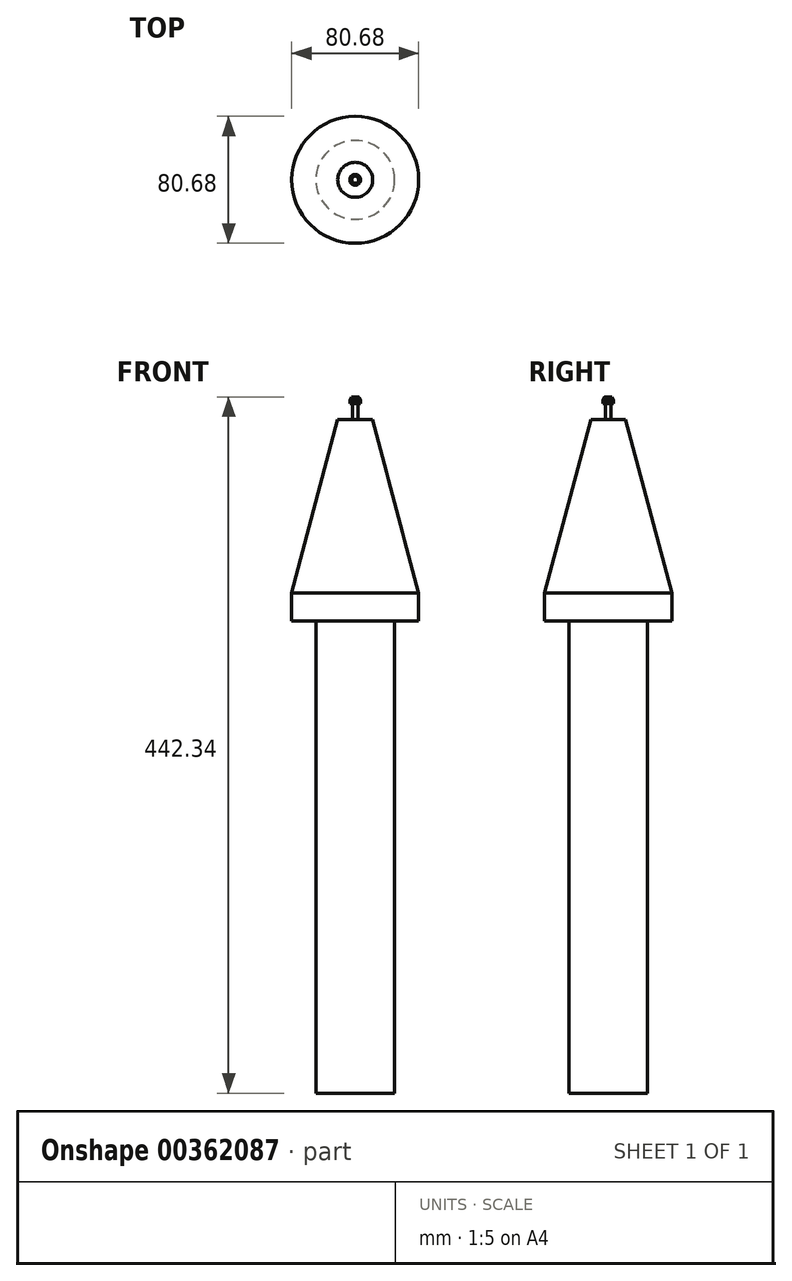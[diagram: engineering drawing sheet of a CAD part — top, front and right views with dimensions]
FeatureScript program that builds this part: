
annotation { "Feature Type Name" : "Feature", "Feature Type Description" : "" }
export const myFeature = defineFeature(function(context is Context, id is Id, definition is map)
    precondition{}
    {
        {
            var Q0;
            Q0=qCreatedBy(makeId("Front.planeOp"),FACE);
            var sketch = newSketch(context, id + "F0", { "sketchPlane" : qUnion([Q0])});
            skLineSegment(sketch, "E0", {"start": v(0, -215.17) * mm, "end": v(25, -215.17) * mm});
            skLineSegment(sketch, "E1", {"start": v(25, -215.17) * mm, "end": v(25, 84.83) * mm});
            skLineSegment(sketch, "E2", {"start": v(25, 84.83) * mm, "end": v(40.34, 84.83) * mm});
            skLineSegment(sketch, "E3", {"start": v(0, 212.9) * mm, "end": v(0, -215.17) * mm});
            skPoint(sketch, "E4.orphan", {"position": v(2.47, 236.47) * mm});
            skPoint(sketch, "E5.end.orphan", {"position": v(4.76, 236.47) * mm});
            skPoint(sketch, "E6.end.orphan", {"position": v(7.06, 236.47) * mm});
            skPoint(sketch, "E7.end.orphan", {"position": v(4.76, 212.9) * mm});
            skLineSegment(sketch, "E8", {"start": v(1.81, 212.9) * mm, "end": v(11.1, 212.9) * mm});
            skLineSegment(sketch, "E9", {"start": v(40.34, 102.43) * mm, "end": v(11.1, 212.9) * mm});
            skLineSegment(sketch, "E10", {"start": v(0, 227.17) * mm, "end": v(0, 212.9) * mm});
            skLineSegment(sketch, "E11", {"start": v(0, 227.17) * mm, "end": v(2.26, 227.17) * mm});
            skLineSegment(sketch, "E12", {"start": v(2.26, 227.17) * mm, "end": v(3.44, 224.95) * mm});
            skLineSegment(sketch, "E13", {"start": v(3.44, 224.95) * mm, "end": v(3.44, 222.87) * mm});
            skLineSegment(sketch, "E14", {"start": v(3.44, 222.87) * mm, "end": v(1.81, 222.87) * mm});
            skLineSegment(sketch, "E15", {"start": v(1.81, 222.87) * mm, "end": v(1.81, 212.9) * mm});
            skLineSegment(sketch, "E16", {"start": v(40.34, 84.83) * mm, "end": v(40.34, 102.43) * mm});
            skSolve(sketch);
        }
        {
            var Q0;
            Q0=makeQuery(id+"F0.imprint","IMPRINT",FACE,{"disambiguationData":[TD([[makeQuery(id+"F0.imprint","IMPRINT",EDGE,{"derivedFrom":sQuery(id+"F0.wireOp",EDGE,"E0")}),1.0]])]});
            var Q1;
            Q1=sQuery(id+"F0.wireOp",EDGE,"E3");
            revolve(context, id + "F1", {"entities" : qUnion([Q0]), "axis" : qUnion([Q1]), "revolveType" : RevolveType.FULL});
        }
    });
